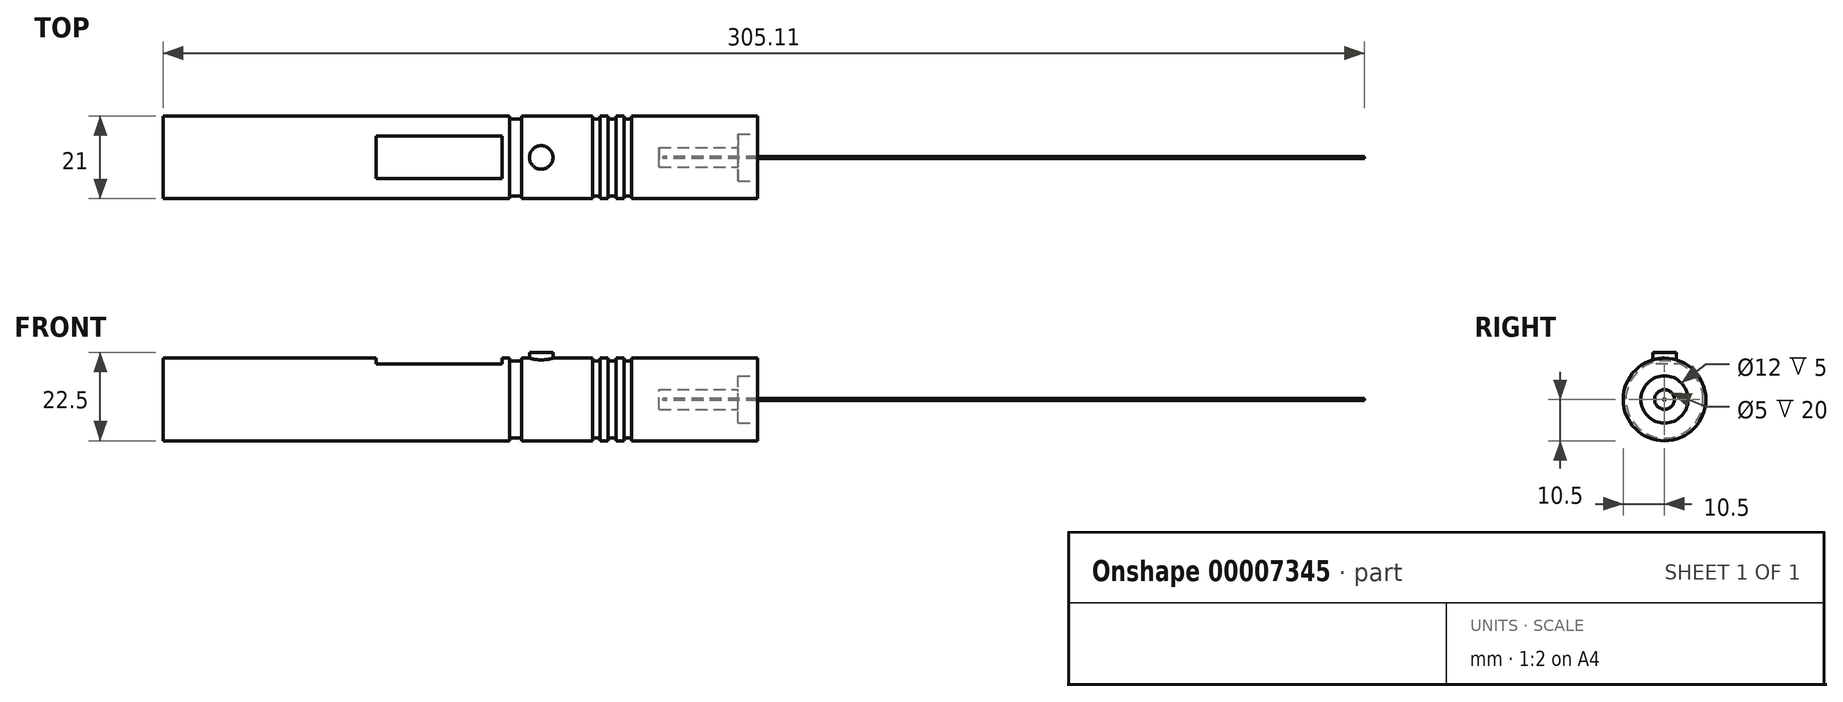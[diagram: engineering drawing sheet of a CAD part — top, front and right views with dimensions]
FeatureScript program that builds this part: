
annotation { "Feature Type Name" : "Feature", "Feature Type Description" : "" }
export const myFeature = defineFeature(function(context is Context, id is Id, definition is map)
    precondition{}
    {
        {
            var Q0;
            Q0=qCreatedBy(makeId("Right.planeOp"),FACE);
            var sketch = newSketch(context, id + "F0", { "sketchPlane" : qUnion([Q0])});
            skCircle(sketch, "E0", {"center": v(0, 0) * mm, "radius": 10.5 * mm});
            skSolve(sketch);
        }
        {
            var Q0;
            Q0=makeQuery(id+"F0.imprint","IMPRINT",FACE,{"disambiguationData":[TD([[makeQuery(id+"F0.imprint","IMPRINT",EDGE,{"derivedFrom":sQuery(id+"F0.wireOp",EDGE,"E0")}),1.0]])]});
            extrude(context, id + "F1", {"entities" : qUnion([Q0]), "endBound" : BoundingType.SYMMETRIC, "depth" : 151 * mm});
        }
        {
            var Q0;
            Q0=qCreatedBy(makeId("Top.planeOp"),FACE);
            cPlane(context, id + "F2", {"entities" : qUnion([Q0]), "cplaneType" : CPlaneType.OFFSET, "offset" : 9 * mm, "width" : 150 * mm, "height" : 150 * mm});
        }
        {
            var Q0;
            Q0=qCreatedBy(id+"F2.planeOp",FACE);
            var sketch = newSketch(context, id + "F3", { "sketchPlane" : qUnion([Q0])});
            skLineSegment(sketch, "E1.bottom", {"start": v(-21.5, 10) * mm, "end": v(10.5, 10) * mm});
            skLineSegment(sketch, "E1.top", {"start": v(-21.5, -10) * mm, "end": v(10.5, -10) * mm});
            skLineSegment(sketch, "E1.left", {"start": v(-21.5, 10) * mm, "end": v(-21.5, -10) * mm});
            skLineSegment(sketch, "E1.right", {"start": v(10.5, 10) * mm, "end": v(10.5, -10) * mm});
            skCircle(sketch, "E2", {"center": v(20.5, 0) * mm, "radius": 3 * mm});
            skSolve(sketch);
        }
        {
            var Q0;
            Q0=makeQuery(id+"F3.imprint","IMPRINT",FACE,{"disambiguationData":[TD([[makeQuery(id+"F3.imprint","IMPRINT",EDGE,{"derivedFrom":sQuery(id+"F3.wireOp",EDGE,"E2")}),1.0]])]});
            var Q1;
            Q1=sQuery(id+"F3.wireOp",EDGE,"E2");
            extrude(context, id + "F4", {"entities" : qUnion([Q0]), "operationType" : NewBodyOperationType.ADD, "surfaceEntities" : qUnion([Q1]), "depth" : 3 * mm});
        }
        {
            var Q0;
            Q0=makeQuery(id+"F3.imprint","IMPRINT",FACE,{"disambiguationData":[TD([[makeQuery(id+"F3.imprint","IMPRINT",EDGE,{"derivedFrom":sQuery(id+"F3.wireOp",EDGE,"E1.bottom")}),-1.0]])]});
            extrude(context, id + "F5", {"entities" : qUnion([Q0]), "operationType" : NewBodyOperationType.REMOVE, "depth" : 5 * mm});
        }
        {
            var Q0;
            Q0=qCreatedBy(makeId("Front.planeOp"),FACE);
            var sketch = newSketch(context, id + "F6", { "sketchPlane" : qUnion([Q0])});
            skLineSegment(sketch, "E3.bottom", {"start": v(12.5, 14) * mm, "end": v(15.5, 14) * mm});
            skLineSegment(sketch, "E3.top", {"start": v(12.5, 9.8) * mm, "end": v(15.5, 9.8) * mm});
            skLineSegment(sketch, "E3.left", {"start": v(12.5, 14) * mm, "end": v(12.5, 9.8) * mm});
            skLineSegment(sketch, "E3.right", {"start": v(15.5, 14) * mm, "end": v(15.5, 9.8) * mm});
            skLineSegment(sketch, "E4.bottom", {"start": v(33.5, 14) * mm, "end": v(35.5, 14) * mm});
            skLineSegment(sketch, "E4.top", {"start": v(33.5, 9.8) * mm, "end": v(35.5, 9.8) * mm});
            skLineSegment(sketch, "E4.left", {"start": v(33.5, 14) * mm, "end": v(33.5, 9.8) * mm});
            skLineSegment(sketch, "E4.right", {"start": v(35.5, 14) * mm, "end": v(35.5, 9.8) * mm});
            skLineSegment(sketch, "E5.bottom", {"start": v(37.5, 14) * mm, "end": v(39.5, 14) * mm});
            skLineSegment(sketch, "E5.top", {"start": v(37.5, 9.8) * mm, "end": v(39.5, 9.8) * mm});
            skLineSegment(sketch, "E5.left", {"start": v(37.5, 14) * mm, "end": v(37.5, 9.8) * mm});
            skLineSegment(sketch, "E5.right", {"start": v(39.5, 14) * mm, "end": v(39.5, 9.8) * mm});
            skLineSegment(sketch, "E6.bottom", {"start": v(41.5, 14) * mm, "end": v(43.5, 14) * mm});
            skLineSegment(sketch, "E6.top", {"start": v(41.5, 9.8) * mm, "end": v(43.5, 9.8) * mm});
            skLineSegment(sketch, "E6.left", {"start": v(41.5, 14) * mm, "end": v(41.5, 9.8) * mm});
            skLineSegment(sketch, "E6.right", {"start": v(43.5, 14) * mm, "end": v(43.5, 9.8) * mm});
            skLineSegment(sketch, "E7", {"start": v(0, 0) * mm, "end": v(113.63, 0) * mm, "construction": true});
            skSolve(sketch);
        }
        {
            var Q0;
            Q0 = qSketchRegion(id + "F6", true);
            var Q1;
            Q1=sQuery(id+"F6.wireOp",EDGE,"E7");
            revolve(context, id + "F7", {"operationType" : NewBodyOperationType.REMOVE, "entities" : qUnion([Q0]), "axis" : qUnion([Q1]), "revolveType" : RevolveType.FULL, "oppositeDirection" : true});
        }
        {
            var Q0;
            Q0=makeQuery(id+"F1.opExtrude","CAP_FACE",FACE,{"disambiguationData":[OSD([sQuery(id+"F0.wireOp",EDGE,"E0")])],"isStart":false});
            var sketch = newSketch(context, id + "F8", { "sketchPlane" : qUnion([Q0])});
            skCircle(sketch, "E8", {"center": v(0, 0) * mm, "radius": 6 * mm});
            skCircle(sketch, "E9", {"center": v(0, 0) * mm, "radius": 2.5 * mm});
            skCircle(sketch, "E10", {"center": v(0, 0) * mm, "radius": 0.25 * mm});
            skSolve(sketch);
        }
        {
            var Q0;
            Q0=makeQuery(id+"F8.imprint","IMPRINT",FACE,{"disambiguationData":[TD([[makeQuery(id+"F8.imprint","IMPRINT",EDGE,{"derivedFrom":sQuery(id+"F8.wireOp",EDGE,"E8")}),1.0]])]});
            var Q1;
            Q1=makeQuery(id+"F8.imprint","IMPRINT",FACE,{"disambiguationData":[TD([[makeQuery(id+"F8.imprint","IMPRINT",EDGE,{"derivedFrom":sQuery(id+"F8.wireOp",EDGE,"E9")}),1.0]])]});
            var Q2;
            Q2=makeQuery(id+"F8.imprint","IMPRINT",FACE,{"disambiguationData":[TD([[makeQuery(id+"F8.imprint","IMPRINT",EDGE,{"derivedFrom":sQuery(id+"F8.wireOp",EDGE,"E10")}),1.0]])]});
            extrude(context, id + "F9", {"entities" : qUnion([Q0, Q1, Q2]), "operationType" : NewBodyOperationType.REMOVE, "oppositeDirection" : true, "depth" : 5 * mm});
        }
        {
            var Q0;
            Q0=makeQuery(id+"F8.imprint","IMPRINT",FACE,{"disambiguationData":[TD([[makeQuery(id+"F8.imprint","IMPRINT",EDGE,{"derivedFrom":sQuery(id+"F8.wireOp",EDGE,"E9")}),1.0]])]});
            var Q1;
            Q1=makeQuery(id+"F8.imprint","IMPRINT",FACE,{"disambiguationData":[TD([[makeQuery(id+"F8.imprint","IMPRINT",EDGE,{"derivedFrom":sQuery(id+"F8.wireOp",EDGE,"E10")}),1.0]])]});
            extrude(context, id + "F10", {"entities" : qUnion([Q0, Q1]), "operationType" : NewBodyOperationType.REMOVE, "oppositeDirection" : true, "depth" : 25 * mm});
        }
        {
            var Q0;
            Q0=makeQuery(id+"F8.imprint","IMPRINT",FACE,{"disambiguationData":[TD([[makeQuery(id+"F8.imprint","IMPRINT",EDGE,{"derivedFrom":sQuery(id+"F8.wireOp",EDGE,"E10")}),1.0]])]});
            var Q1;
            Q1=sQuery(id+"F8.wireOp",EDGE,"E10");
            extrude(context, id + "F11", {"entities" : qUnion([Q0]), "surfaceEntities" : qUnion([Q1]), "endBound" : BoundingType.THROUGH_ALL, "depth" : 25 * mm, "hasSecondDirection" : true, "secondDirectionOppositeDirection" : true, "secondDirectionDepth" : 24 * mm});
        }
    });
